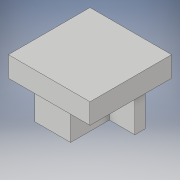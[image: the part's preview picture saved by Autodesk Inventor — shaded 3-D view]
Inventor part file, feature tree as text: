
AUTODESK INVENTOR PART (.ipt)
format: ipt  version: 2019 (Build 230136000, 136)  size: 115,712 bytes
history: native  units: mm
features: extrude x2, sketch x1
ambient origin geometry x8: Origin, YZ Plane, XZ Plane, XY Plane, X Axis, Y Axis, Z Axis, Center Point
bodies: Solid1 (feature_tree)
feature tree (3):
  sketch  "Sketch1"  dims[d0=20.0mm d1=20.0mm d2=2.5mm d3=2.5mm d4=12.0mm d5=2.5mm d6=2.5mm d7=2.5mm d8=10.0mm d9=0.0mm d10=5.0mm d11=0.0mm]
  extrude  "Extrusion1"  Depth=20.0mm
  extrude  "Extrusion2"  Depth=2.5mm
